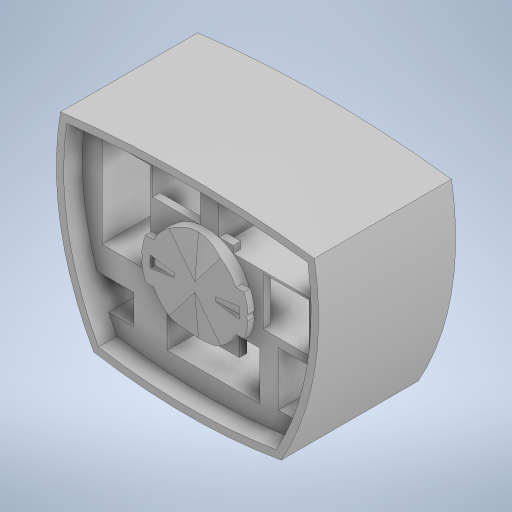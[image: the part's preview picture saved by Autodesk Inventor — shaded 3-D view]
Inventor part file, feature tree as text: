
AUTODESK INVENTOR PART (.ipt)
format: ipt  version: 2023 (Build 270158000, 158)  size: 660,992 bytes
history: mixed  units: in
note: dims shown in document units (in); Inventor stores cm internally (conversion verified against a paired STEP export)
features: extrude x12, projected_geometry x11, sketch x5, imported_body x1
ambient origin geometry x8: Origin, YZ Plane, XZ Plane, XY Plane, X Axis, Y Axis, Z Axis, Center Point
bodies: Solid1 (imported_parasolid), Body1 (imported_parasolid)
feature tree (29):
  extrude  "Extrusion5"  Depth=0.9055in
  sketch  "Sketch5"  dims[d13=0.9843in d18=2.5591in]
  extrude  "Extrusion6"  Depth=0.9843in
  extrude  "Extrusion7"  Depth=0.0787in
  extrude  "Extrusion8"  Depth=1.2795in
  extrude  "Extrusion12"  Depth=0.0787in
  sketch  "Sketch10"  dims[d21=1.2795in d22=1.2795in]
  extrude  "Extrusion14"  Depth=0.0787in
  extrude  "Extrusion17"  Depth=1.8898in
  extrude  "Extrusion18"  Depth=0.0787in TaperAngle=0.0deg
  extrude  "Extrusion19"  Depth=0.7874in TaperAngle=0.0deg
  extrude  "Extrusion20"  Depth=0.0787in TaperAngle=0.0deg
  extrude  "Extrusion21"  Depth=0.0787in TaperAngle=0.0deg
  extrude  "Extrusion22"  Depth=0.0787in
  sketch  "Sketch1"  dims[d10=0.3937in d11=0.0in d12=0.9055in]
  sketch  "Sketch8"  dims[d19=0.0787in d20=0.0787in]
  sketch  "Sketch12"  dims[d23=0.0787in d24=0.0787in d25=2.5591in d26=1.8898in d27=0.0787in d28=0.0in d29=0.7874in d30=0.0in d31=0.6693in d32=0.0in d54=0.0787in d55=0.0in d66=1.2992in d123=0.7874in d124=0.0in d136=0.4724in d137=0.0in d141=0.4724in d142=0.0in d144=1.2992in d145=0.5118in d146=0.5118in d147=0.0242in d150=0.1575in d152=0.1181in d153=0.1575in d154=0.1181in d155=0.1575in d156=0.1575in d157=0.1181in d158=0.1181in d159=1.2992in d160=0.5118in d161=0.0in d166=1.2992in d168=0.5118in d169=0.5118in d171=1.2992in d172=0.5118in d174=0.1575in d175=0.1575in d176=0.1181in d177=0.1181in d178=0.315in d179=0.1575in d180=0.1181in d181=0.1575in d182=0.1181in d183=0.1575in d184=0.1181in d185=0.1575in d186=0.1181in d187=0.7087in d188=0.0in d189=0.7087in d190=0.0in d191=0.1969in d192=0.0787in d193=0.0in d194=0.0787in d195=0.0in d0=0.0197in d1=1.9685in d2=0.0197in d3=1.9685in d125=0.0197in d126=0.0344in d127=0.0197in d128=0.0344in]
  projected_geometry  "Projected Loop6"
  projected_geometry  "Projected Loop7"
  projected_geometry  "Projected Loop8"
  projected_geometry  "Projected Loop9"
  projected_geometry  "Projected Loop10"
  projected_geometry  "Projected Loop11"
  projected_geometry  "Projected Loop12"
  projected_geometry  "Projected Loop13"
  projected_geometry  "Projected Loop14"
  projected_geometry  "Projected Loop15"
  projected_geometry  "Projected Loop16"
  imported_body  NMx_Import_Brep_tag  [imported B-rep: ~75 faces, bbox_mm=[68.464898, 51.606881, 37.0]]
